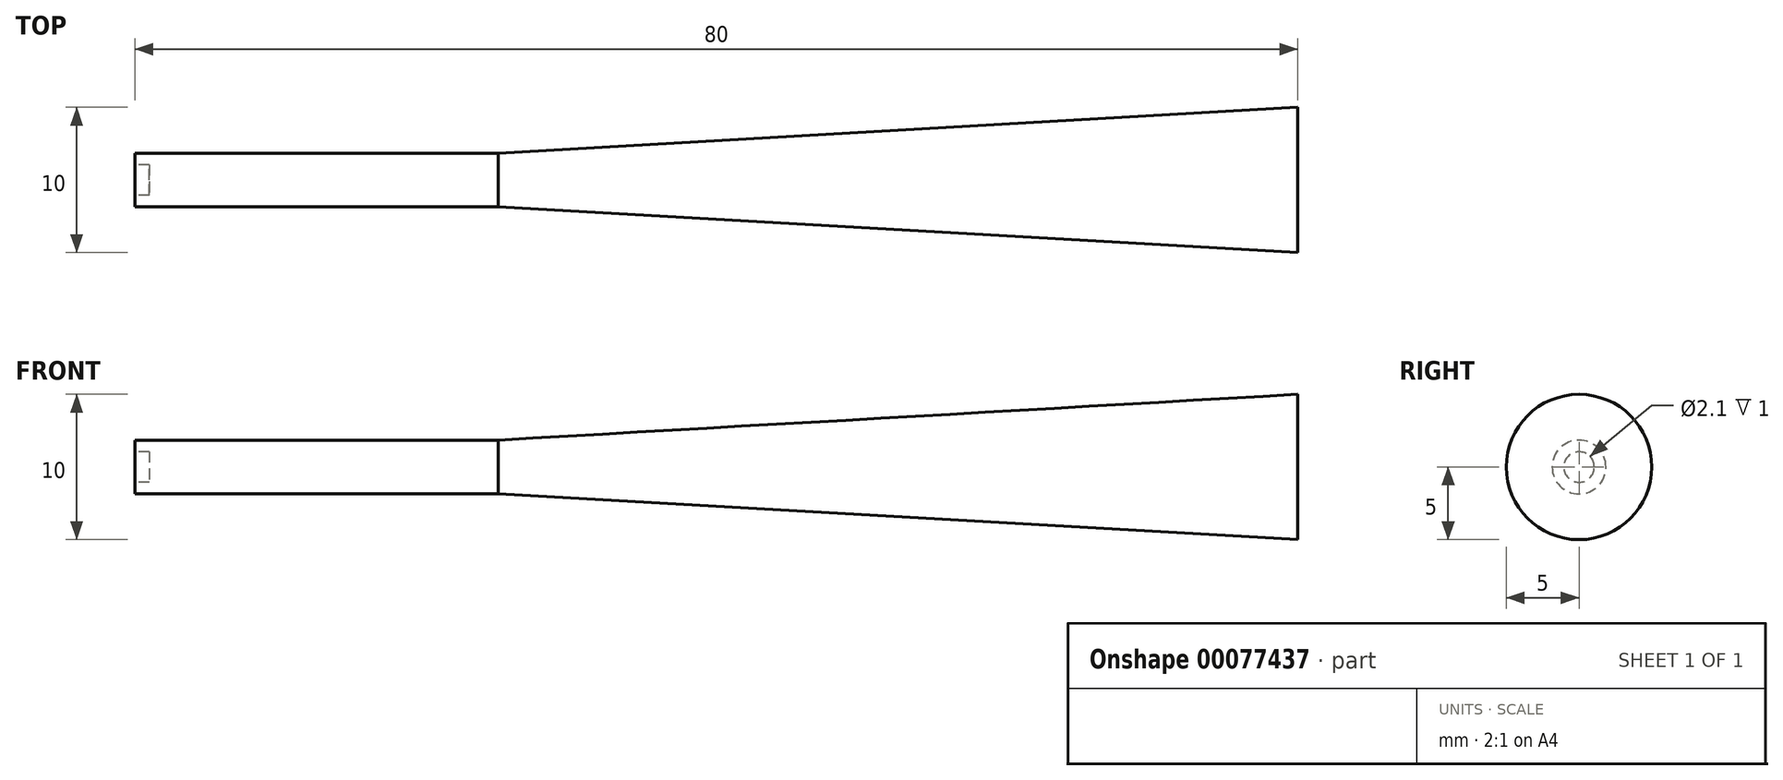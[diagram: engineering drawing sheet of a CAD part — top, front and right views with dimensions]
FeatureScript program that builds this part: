
annotation { "Feature Type Name" : "Feature", "Feature Type Description" : "" }
export const myFeature = defineFeature(function(context is Context, id is Id, definition is map)
    precondition{}
    {
        {
            var Q0;
            Q0=qCreatedBy(makeId("Front.planeOp"),FACE);
            var sketch = newSketch(context, id + "F0", { "sketchPlane" : qUnion([Q0])});
            skLineSegment(sketch, "E0", {"start": v(0, 0) * mm, "end": v(12.7, 0) * mm});
            skLineSegment(sketch, "E1", {"start": v(0, 1.05) * mm, "end": v(1, 1.05) * mm});
            skLineSegment(sketch, "E2", {"start": v(1, 1.05) * mm, "end": v(1, 0) * mm});
            skLineSegment(sketch, "E3", {"start": v(1, 0) * mm, "end": v(80, 0) * mm});
            skLineSegment(sketch, "E4", {"start": v(80, 0) * mm, "end": v(80, 5) * mm});
            skLineSegment(sketch, "E5", {"start": v(80, 5) * mm, "end": v(25, 1.85) * mm});
            skLineSegment(sketch, "E6", {"start": v(25, 1.85) * mm, "end": v(0, 1.85) * mm});
            skLineSegment(sketch, "E7", {"start": v(0, 1.85) * mm, "end": v(0, 1.05) * mm});
            skLineSegment(sketch, "E8.MirrorCS", {"start": v(1, -1.05) * mm, "end": v(1, 0) * mm});
            skLineSegment(sketch, "E9.MirrorCS", {"start": v(0, -1.05) * mm, "end": v(1, -1.05) * mm});
            skLineSegment(sketch, "E10.MirrorCS", {"start": v(0, -1.85) * mm, "end": v(0, -1.05) * mm});
            skLineSegment(sketch, "E11.MirrorCS", {"start": v(25, -1.85) * mm, "end": v(0, -1.85) * mm});
            skLineSegment(sketch, "E12.MirrorCS", {"start": v(80, -5) * mm, "end": v(25, -1.85) * mm});
            skLineSegment(sketch, "E13.MirrorCS", {"start": v(80, 0) * mm, "end": v(80, -5) * mm});
            skSolve(sketch);
        }
        {
            var Q0;
            Q0=makeQuery(id+"F0.imprint","IMPRINT",FACE,{"disambiguationData":[TD([[makeQuery(id+"F0.imprint","IMPRINT",EDGE,{"derivedFrom":sQuery(id+"F0.wireOp",EDGE,"E1")}),1.0]])]});
            var Q1;
            Q1=sQuery(id+"F0.wireOp",EDGE,"E3");
            revolve(context, id + "F1", {"entities" : qUnion([Q0]), "axis" : qUnion([Q1]), "revolveType" : RevolveType.FULL});
        }
    });
